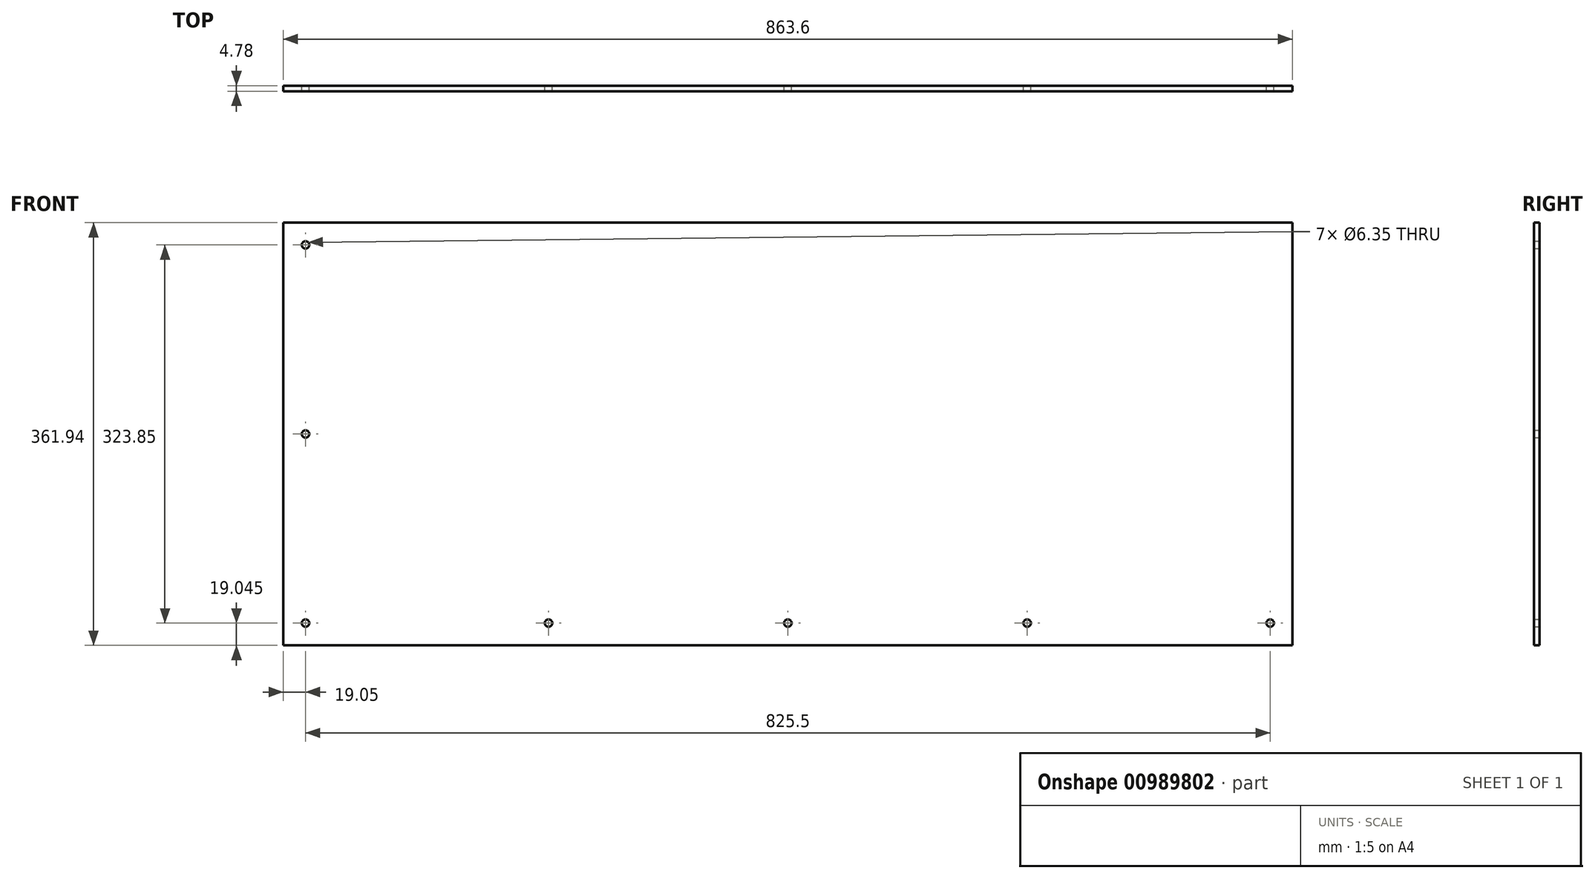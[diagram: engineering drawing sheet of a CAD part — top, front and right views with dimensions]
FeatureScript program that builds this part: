
annotation { "Feature Type Name" : "Feature", "Feature Type Description" : "" }
export const myFeature = defineFeature(function(context is Context, id is Id, definition is map)
    precondition{}
    {
        {
            var Q0;
            Q0=qCreatedBy(makeId("Front.planeOp"),FACE);
            var sketch = newSketch(context, id + "F0", { "sketchPlane" : qUnion([Q0])});
            skLineSegment(sketch, "E0.bottom", {"start": v(-431.8, 180.98) * mm, "end": v(431.8, 180.98) * mm});
            skLineSegment(sketch, "E0.top", {"start": v(-431.8, -180.98) * mm, "end": v(431.8, -180.98) * mm});
            skLineSegment(sketch, "E0.left", {"start": v(-431.8, 180.98) * mm, "end": v(-431.8, -180.98) * mm});
            skLineSegment(sketch, "E0.right", {"start": v(431.8, 180.98) * mm, "end": v(431.8, -180.98) * mm});
            skCircle(sketch, "E1", {"center": v(-412.75, -161.93) * mm, "radius": 3.18 * mm});
            skCircle(sketch, "E2.0.1.0", {"center": v(-412.75, 0) * mm, "radius": 3.18 * mm});
            skCircle(sketch, "E2.0.2.0", {"center": v(-412.75, 161.93) * mm, "radius": 3.18 * mm});
            skLineSegment(sketch, "E2.direction1", {"start": v(-412.75, -161.93) * mm, "end": v(-412.75, -161.93) * mm});
            skLineSegment(sketch, "E2.direction2", {"start": v(-412.75, -161.93) * mm, "end": v(-412.75, 0) * mm, "construction": true});
            skCircle(sketch, "E3.1.0.0", {"center": v(-204.79, -161.93) * mm, "radius": 3.18 * mm});
            skLineSegment(sketch, "E3.direction1", {"start": v(-412.75, -161.93) * mm, "end": v(-204.79, -161.93) * mm, "construction": true});
            skCircle(sketch, "E4.1.0.0", {"center": v(0, -161.93) * mm, "radius": 3.18 * mm});
            skCircle(sketch, "E4.2.0.0", {"center": v(204.79, -161.93) * mm, "radius": 3.18 * mm});
            skLineSegment(sketch, "E4.direction1", {"start": v(-204.79, -161.93) * mm, "end": v(0, -161.93) * mm, "construction": true});
            skCircle(sketch, "E5.1.0.0", {"center": v(412.75, -161.93) * mm, "radius": 3.18 * mm});
            skLineSegment(sketch, "E5.direction1", {"start": v(204.79, -161.93) * mm, "end": v(412.75, -161.93) * mm, "construction": true});
            skSolve(sketch);
        }
        {
            var Q0;
            Q0=makeQuery(id+"F0.imprint","IMPRINT",FACE,{"disambiguationData":[TD([[makeQuery(id+"F0.imprint","IMPRINT",EDGE,{"derivedFrom":sQuery(id+"F0.wireOp",EDGE,"E0.bottom")}),-1.0]])]});
            extrude(context, id + "F1", {"entities" : qUnion([Q0]), "depth" : 4.78 * mm, "offsetDistance" : 25.4 * mm});
        }
    });
